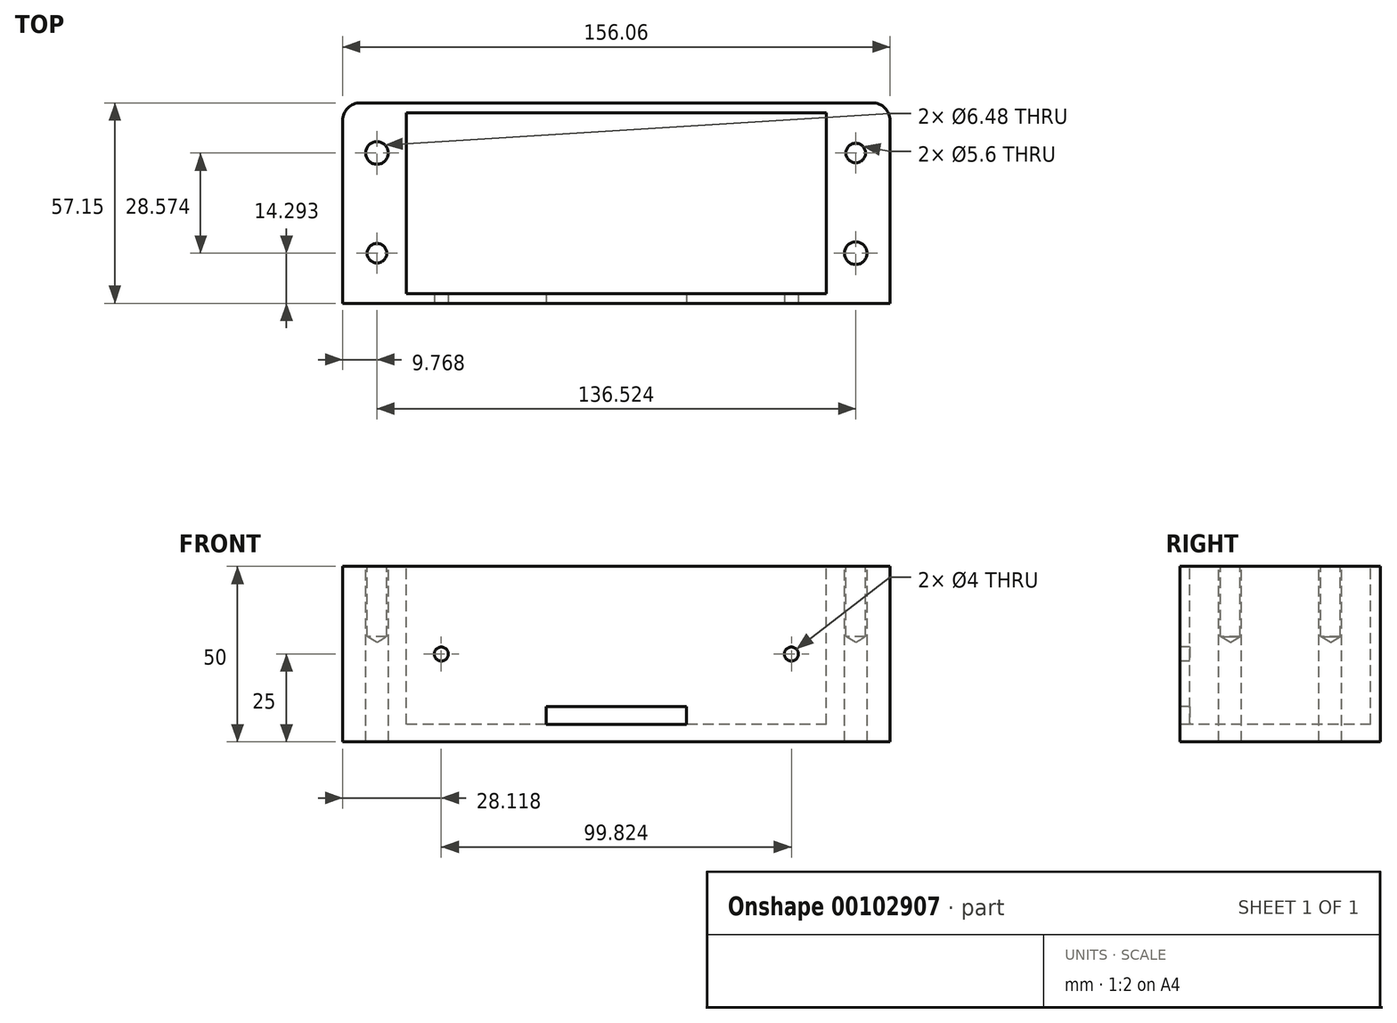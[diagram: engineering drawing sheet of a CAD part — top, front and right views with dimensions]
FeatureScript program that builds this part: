
annotation { "Feature Type Name" : "Feature", "Feature Type Description" : "" }
export const myFeature = defineFeature(function(context is Context, id is Id, definition is map)
    precondition{}
    {
        {
            var Q0;
            Q0=qCreatedBy(makeId("Top.planeOp"),FACE);
            var sketch = newSketch(context, id + "F0", { "sketchPlane" : qUnion([Q0])});
            skLineSegment(sketch, "E0", {"start": v(-68.26, 20.64) * mm, "end": v(-72.23, 20.64) * mm});
            skLineSegment(sketch, "E1", {"start": v(-72.23, 20.64) * mm, "end": v(-72.23, 27.78) * mm});
            skArc(sketch, "E2", {"start": v(-68.26, 7.94) * mm, "mid": v(-61.91, 14.29) * mm, "end": v(-68.26, 20.64) * mm});
            skLineSegment(sketch, "E3", {"start": v(-68.26, 7.94) * mm, "end": v(-72.23, 7.94) * mm});
            skLineSegment(sketch, "E4", {"start": v(-72.23, -7.94) * mm, "end": v(-72.23, 7.94) * mm});
            skLineSegment(sketch, "E5", {"start": v(72.22, 20.64) * mm, "end": v(72.22, 27.78) * mm});
            skLineSegment(sketch, "E6", {"start": v(72.22, 27.78) * mm, "end": v(-72.22, 27.78) * mm});
            skLineSegment(sketch, "E7", {"start": v(72.22, -7.94) * mm, "end": v(72.22, 7.94) * mm});
            skArc(sketch, "E8", {"start": v(68.18, -7.94) * mm, "mid": v(61.91, -14.37) * mm, "end": v(68.35, -20.64) * mm});
            skLineSegment(sketch, "E9", {"start": v(68.18, -7.94) * mm, "end": v(72.22, -7.94) * mm});
            skLineSegment(sketch, "E10", {"start": v(72.22, -27.78) * mm, "end": v(72.22, -20.64) * mm});
            skLineSegment(sketch, "E11", {"start": v(68.35, -20.64) * mm, "end": v(72.22, -20.64) * mm});
            skLineSegment(sketch, "E12", {"start": v(-72.23, -27.78) * mm, "end": v(-72.23, -20.64) * mm});
            skLineSegment(sketch, "E13", {"start": v(-72.23, -27.78) * mm, "end": v(72.22, -27.78) * mm});
            skCircle(sketch, "E14", {"center": v(68.26, -14.29) * mm, "radius": 3.24 * mm});
            skCircle(sketch, "E15", {"center": v(-68.26, 14.29) * mm, "radius": 3.24 * mm});
            skLineSegment(sketch, "E16", {"start": v(-73.03, 28.57) * mm, "end": v(73.02, 28.57) * mm});
            skLineSegment(sketch, "E17", {"start": v(-73.03, -28.57) * mm, "end": v(-73.03, 28.57) * mm});
            skLineSegment(sketch, "E18", {"start": v(73.03, -28.57) * mm, "end": v(-73.02, -28.57) * mm});
            skLineSegment(sketch, "E19", {"start": v(73.03, 28.57) * mm, "end": v(73.03, -28.57) * mm});
            skCircle(sketch, "E20.MirrorC", {"center": v(68.26, 14.29) * mm, "radius": 3.24 * mm});
            skArc(sketch, "E21.MirrorCS", {"start": v(68.26, 7.94) * mm, "mid": v(61.91, 14.29) * mm, "end": v(68.26, 20.64) * mm});
            skLineSegment(sketch, "E22.MirrorCS", {"start": v(68.26, 20.64) * mm, "end": v(72.23, 20.64) * mm});
            skLineSegment(sketch, "E23.MirrorCS", {"start": v(68.26, 7.94) * mm, "end": v(72.23, 7.94) * mm});
            skLineSegment(sketch, "E24.MirrorCS", {"start": v(-68.26, -20.64) * mm, "end": v(-72.23, -20.64) * mm});
            skArc(sketch, "E25.MirrorCS", {"start": v(-68.26, -7.94) * mm, "mid": v(-61.91, -14.29) * mm, "end": v(-68.26, -20.64) * mm});
            skCircle(sketch, "E26.MirrorC", {"center": v(-68.26, -14.29) * mm, "radius": 3.24 * mm});
            skLineSegment(sketch, "E27.MirrorCS", {"start": v(-68.26, -7.94) * mm, "end": v(-72.23, -7.94) * mm});
            skLineSegment(sketch, "E28.bottom", {"start": v(73.02, 28.57) * mm, "end": v(78.02, 28.57) * mm});
            skLineSegment(sketch, "E28.top", {"start": v(73.02, -28.57) * mm, "end": v(78.02, -28.57) * mm});
            skLineSegment(sketch, "E28.left", {"start": v(73.02, 28.57) * mm, "end": v(73.02, -28.57) * mm});
            skLineSegment(sketch, "E28.right", {"start": v(78.02, 28.57) * mm, "end": v(78.02, -28.57) * mm});
            skLineSegment(sketch, "E29.MirrorCS", {"start": v(-73.02, -28.57) * mm, "end": v(-78.02, -28.57) * mm});
            skLineSegment(sketch, "E30.MirrorCS", {"start": v(-78.02, 28.57) * mm, "end": v(-78.02, -28.57) * mm});
            skLineSegment(sketch, "E31.MirrorCS", {"start": v(-73.02, 28.57) * mm, "end": v(-78.02, 28.57) * mm});
            skSolve(sketch);
        }
        {
            var Q0;
            Q0=qSketchRegion(id+"F0",true);
            var Q1;
            Q1=makeQuery(id+"F0.imprint","IMPRINT",FACE,{"disambiguationData":[TD([[makeQuery(id+"F0.imprint","IMPRINT",EDGE,{"derivedFrom":sQuery(id+"F0.wireOp",EDGE,"E15")}),-1.0]])]});
            var Q2;
            Q2=makeQuery(id+"F0.imprint","IMPRINT",FACE,{"disambiguationData":[TD([[makeQuery(id+"F0.imprint","IMPRINT",EDGE,{"derivedFrom":sQuery(id+"F0.wireOp",EDGE,"E2")}),-1.0]])]});
            var Q3;
            Q3=makeQuery(id+"F0.imprint","IMPRINT",FACE,{"disambiguationData":[TD([[makeQuery(id+"F0.imprint","IMPRINT",EDGE,{"derivedFrom":sQuery(id+"F0.wireOp",EDGE,"E26.MirrorC")}),1.0]])]});
            var Q4;
            Q4=makeQuery(id+"F0.imprint","IMPRINT",FACE,{"disambiguationData":[TD([[makeQuery(id+"F0.imprint","IMPRINT",EDGE,{"derivedFrom":sQuery(id+"F0.wireOp",EDGE,"E20.MirrorC")}),1.0]])]});
            var Q5;
            Q5=makeQuery(id+"F0.imprint","IMPRINT",FACE,{"disambiguationData":[TD([[makeQuery(id+"F0.imprint","IMPRINT",EDGE,{"derivedFrom":sQuery(id+"F0.wireOp",EDGE,"E14")}),-1.0]])]});
            extrude(context, id + "F1", {"entities" : qUnion([Q0, Q1, Q2, Q3, Q4, Q5]), "oppositeDirection" : true, "depth" : 50 * mm});
        }
        {
            var Q0;
            Q0=makeQuery(id+"F1.opExtrude","CAP_FACE",FACE,{"disambiguationData":[OSD([sQuery(id+"F0.wireOp",EDGE,"E16"),sQuery(id+"F0.wireOp",EDGE,"E18"),sQuery(id+"F0.wireOp",EDGE,"E28.bottom"),sQuery(id+"F0.wireOp",EDGE,"E28.top"),sQuery(id+"F0.wireOp",EDGE,"E28.right"),sQuery(id+"F0.wireOp",EDGE,"E29.MirrorCS"),sQuery(id+"F0.wireOp",EDGE,"E30.MirrorCS"),sQuery(id+"F0.wireOp",EDGE,"E31.MirrorCS")])],"isStart":true});
            var sketch = newSketch(context, id + "F2", { "sketchPlane" : qUnion([Q0])});
            skLineSegment(sketch, "E32.bottom", {"start": v(59.91, 25.78) * mm, "end": v(-59.91, 25.78) * mm});
            skLineSegment(sketch, "E32.top", {"start": v(59.91, -25.78) * mm, "end": v(-59.91, -25.78) * mm});
            skLineSegment(sketch, "E32.left", {"start": v(59.91, 25.78) * mm, "end": v(59.91, -25.78) * mm});
            skLineSegment(sketch, "E32.right", {"start": v(-59.91, 25.78) * mm, "end": v(-59.91, -25.78) * mm});
            skPoint(sketch, "E32.middle", {"position": v(0, 0) * mm});
            skSolve(sketch);
        }
        {
            var Q0;
            Q0=qSketchRegion(id+"F2",true);
            extrude(context, id + "F3", {"entities" : qUnion([Q0]), "operationType" : NewBodyOperationType.REMOVE, "oppositeDirection" : true, "depth" : 45 * mm});
        }
        {
            var Q0;
            Q0=sQuery(id+"F0.wireOp",VERTEX,"E2.center");
            var Q1;
            Q1=sQuery(id+"F0.wireOp",VERTEX,"E25.MirrorCS.center");
            var Q2;
            Q2=sQuery(id+"F0.wireOp",VERTEX,"E20.MirrorC.center");
            var Q3;
            Q3=sQuery(id+"F0.wireOp",VERTEX,"E8.center");
            var Q4;
            Q4=makeQuery(id+"F1.opExtrude","SWEPT_BODY",BODY,{"disambiguationData":[OSD([sQuery(id+"F0.wireOp",EDGE,"E16"),sQuery(id+"F0.wireOp",EDGE,"E18"),sQuery(id+"F0.wireOp",EDGE,"E28.bottom"),sQuery(id+"F0.wireOp",EDGE,"E28.top"),sQuery(id+"F0.wireOp",EDGE,"E28.right"),sQuery(id+"F0.wireOp",EDGE,"E29.MirrorCS"),sQuery(id+"F0.wireOp",EDGE,"E30.MirrorCS"),sQuery(id+"F0.wireOp",EDGE,"E31.MirrorCS")])]});
            hole(context, id + "F4", {"style" : HoleStyle.SIMPLE, "endStyle" : HoleEndStyle.BLIND, "holeDiameter" : 5.6 * mm, "holeDepth" : 20 * mm, "locations" : qUnion([Q0, Q1, Q2, Q3]), "scope" : qUnion([Q4])});
        }
        {
            var Q0;
            Q0=makeQuery(id+"F1.opExtrude","SWEPT_FACE",FACE,{"disambiguationData":[OSD([sQuery(id+"F0.wireOp",EDGE,"E18"),sQuery(id+"F0.wireOp",EDGE,"E28.top"),sQuery(id+"F0.wireOp",EDGE,"E29.MirrorCS")])]});
            var sketch = newSketch(context, id + "F5", { "sketchPlane" : qUnion([Q0])});
            skLineSegment(sketch, "E33.bottom", {"start": v(20, -40) * mm, "end": v(-20, -40) * mm});
            skLineSegment(sketch, "E33.top", {"start": v(20, -45) * mm, "end": v(-20, -45) * mm});
            skLineSegment(sketch, "E33.left", {"start": v(20, -40) * mm, "end": v(20, -45) * mm});
            skLineSegment(sketch, "E33.right", {"start": v(-20, -40) * mm, "end": v(-20, -45) * mm});
            skPoint(sketch, "E33.middle", {"position": v(0, -42.5) * mm});
            skPoint(sketch, "E34", {"position": v(-49.91, -25) * mm});
            skPoint(sketch, "E35.MirrorP", {"position": v(49.91, -25) * mm});
            skSolve(sketch);
        }
        {
            var Q0;
            Q0=qSketchRegion(id+"F5",true);
            extrude(context, id + "F6", {"entities" : qUnion([Q0]), "operationType" : NewBodyOperationType.REMOVE, "endBound" : BoundingType.UP_TO_NEXT, "oppositeDirection" : true, "depth" : 25 * mm});
        }
        {
            var Q0;
            Q0=sQuery(id+"F5.wireOp",VERTEX,"E34");
            var Q1;
            Q1=sQuery(id+"F5.wireOp",VERTEX,"E35.MirrorP");
            var Q2;
            Q2=makeQuery(id+"F1.opExtrude","SWEPT_BODY",BODY,{"disambiguationData":[OSD([sQuery(id+"F0.wireOp",EDGE,"E16"),sQuery(id+"F0.wireOp",EDGE,"E18"),sQuery(id+"F0.wireOp",EDGE,"E28.bottom"),sQuery(id+"F0.wireOp",EDGE,"E28.top"),sQuery(id+"F0.wireOp",EDGE,"E28.right"),sQuery(id+"F0.wireOp",EDGE,"E29.MirrorCS"),sQuery(id+"F0.wireOp",EDGE,"E30.MirrorCS"),sQuery(id+"F0.wireOp",EDGE,"E31.MirrorCS")])]});
            hole(context, id + "F7", {"style" : HoleStyle.SIMPLE, "endStyle" : HoleEndStyle.BLIND, "holeDiameter" : 4 * mm, "holeDepth" : 20 * mm, "locations" : qUnion([Q0, Q1]), "scope" : qUnion([Q2])});
        }
        {
            var Q0;
            Q0=makeQuery(id+"F1.opExtrude","SWEPT_EDGE",EDGE,{"disambiguationData":[OSD([sQuery(id+"F0.wireOp",EDGE,"E30.MirrorCS"),sQuery(id+"F0.wireOp",EDGE,"E31.MirrorCS")])]});
            var Q1;
            Q1=makeQuery(id+"F1.opExtrude","SWEPT_EDGE",EDGE,{"disambiguationData":[OSD([sQuery(id+"F0.wireOp",EDGE,"E28.bottom"),sQuery(id+"F0.wireOp",EDGE,"E28.right")])]});
            fillet(context, id + "F8", {"entities" : qUnion([Q0, Q1]), "radius" : 5 * mm, "tangentPropagation" : true, "allowEdgeOverflow" : false});
        }
    });
